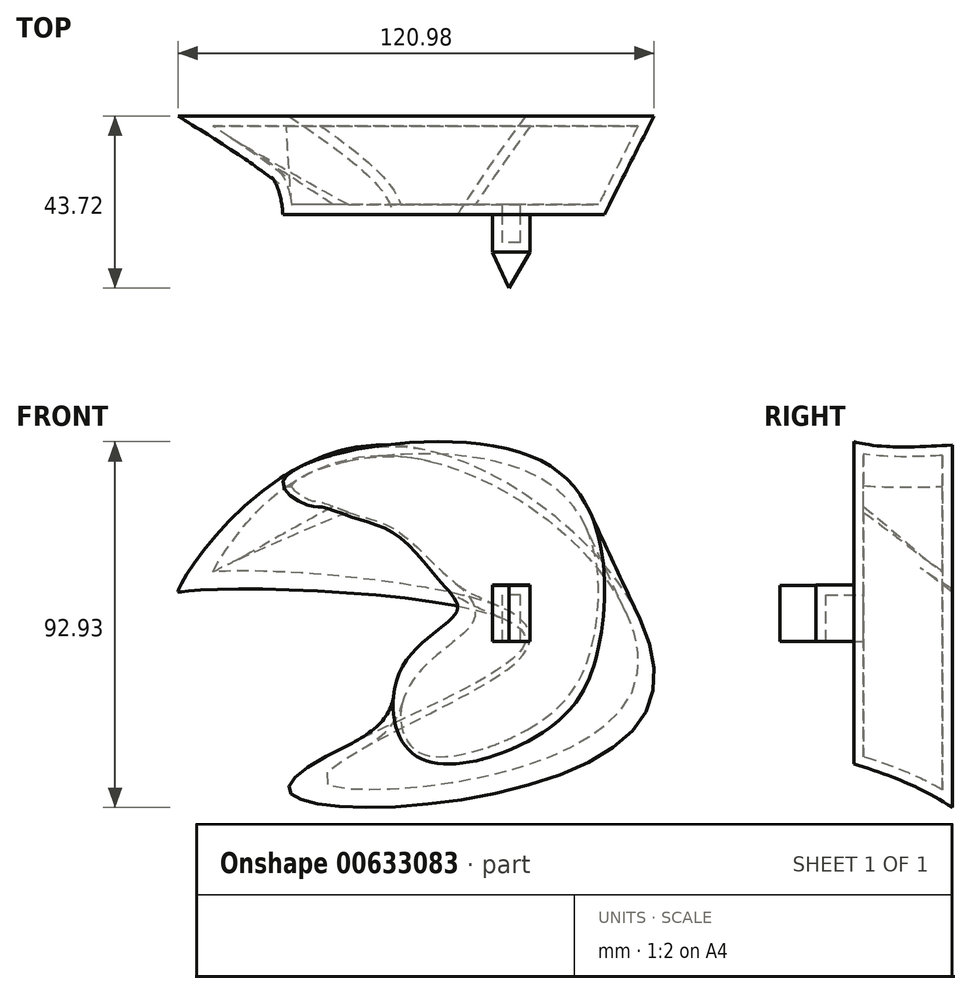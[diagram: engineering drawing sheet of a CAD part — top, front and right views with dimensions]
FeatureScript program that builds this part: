
annotation { "Feature Type Name" : "Feature", "Feature Type Description" : "" }
export const myFeature = defineFeature(function(context is Context, id is Id, definition is map)
    precondition{}
    {
        {
            var Q0;
            Q0=qCreatedBy(makeId("Front.planeOp"),FACE);
            var sketch = newSketch(context, id + "F0", { "sketchPlane" : qUnion([Q0])});
            skFitSpline(sketch, "E0", {"points": [v(-16.33, 40.2) * mm, v(-66.93, 3.34) * mm, v(-63.68, 3.15) * mm, v(21.3, -9.26) * mm, v(-38.86, -46.88) * mm, v(50.89, -29.31) * mm, v(-16.33, 40.2) * mm]});
            skSolve(sketch);
        }
        {
            var Q0;
            Q0=makeQuery(id+"F0.imprint","IMPRINT",FACE,{"disambiguationData":[TD([[makeQuery(id+"F0.imprint","IMPRINT",EDGE,{"derivedFrom":sQuery(id+"F0.wireOp",EDGE,"E0")}),1.0]])]});
            cPlane(context, id + "F1", {"entities" : qUnion([Q0]), "cplaneType" : CPlaneType.OFFSET, "offset" : 25 * mm, "width" : 150 * mm, "height" : 150 * mm});
        }
        {
            var Q0;
            Q0=qCreatedBy(id+"F1.planeOp",FACE);
            var sketch = newSketch(context, id + "F2", { "sketchPlane" : qUnion([Q0])});
            skFitSpline(sketch, "E1", {"points": [v(-40.27, 30.87) * mm, v(24.89, 36.37) * mm, v(40.37, -8.48) * mm, v(25.94, -32.7) * mm, v(-6.61, -38.72) * mm, v(-9.78, -15.81) * mm, v(3.9, -1.9) * mm, v(0, 5.1) * mm, v(-11.63, 17.45) * mm, v(-22.04, 21.6) * mm, v(-30.2, 24.38) * mm, v(-33.32, 24.7) * mm, v(-40.27, 30.87) * mm]});
            skSolve(sketch);
        }
        {
            var Q0;
            Q0=makeQuery(id+"F2.imprint","IMPRINT",FACE,{"disambiguationData":[TD([[makeQuery(id+"F2.imprint","IMPRINT",EDGE,{"derivedFrom":sQuery(id+"F2.wireOp",EDGE,"E1")}),-1.0]])]});
            var Q1;
            Q1=makeQuery(id+"F0.imprint","IMPRINT",FACE,{"disambiguationData":[TD([[makeQuery(id+"F0.imprint","IMPRINT",EDGE,{"derivedFrom":sQuery(id+"F0.wireOp",EDGE,"E0")}),1.0]])]});
            loft(context, id + "F3", {"sheetProfilesArray" : [{ "sheetProfileEntities" : qUnion([Q0]) }, { "sheetProfileEntities" : qUnion([Q1]) }]});
        }
        {
            var Q0;
            Q0=makeQuery(id+"F3.opLoft","CAP_FACE",FACE,{"disambiguationData":[OSD([makeQuery(id+"F2.imprint","IMPRINT",FACE,{"disambiguationData":[TD([[makeQuery(id+"F2.imprint","IMPRINT",EDGE,{"derivedFrom":sQuery(id+"F2.wireOp",EDGE,"E1")}),-1.0]])]})])],"isStart":true});
            var sketch = newSketch(context, id + "F4", { "sketchPlane" : qUnion([Q0])});
            skLineSegment(sketch, "E2.bottom", {"start": v(22.48, -9.74) * mm, "end": v(12.93, -9.74) * mm});
            skLineSegment(sketch, "E2.top", {"start": v(22.48, 4.57) * mm, "end": v(12.93, 4.57) * mm});
            skLineSegment(sketch, "E2.left", {"start": v(22.48, -9.74) * mm, "end": v(22.48, 4.57) * mm});
            skLineSegment(sketch, "E2.right", {"start": v(12.93, -9.74) * mm, "end": v(12.93, 4.57) * mm});
            skSolve(sketch);
        }
        {
            var Q0;
            Q0=makeQuery(id+"F4.imprint","IMPRINT",FACE,{"disambiguationData":[TD([[makeQuery(id+"F4.imprint","IMPRINT",EDGE,{"derivedFrom":sQuery(id+"F4.wireOp",EDGE,"E2.bottom")}),-1.0]])]});
            extrude(context, id + "F5", {"entities" : qUnion([Q0]), "operationType" : NewBodyOperationType.ADD, "depth" : 9.6 * mm, "offsetDistance" : 25 * mm});
        }
        {
            var Q0;
            Q0=makeQuery(id+"F5.opExtrude","SWEPT_FACE",FACE,{"disambiguationData":[OSD([sQuery(id+"F4.wireOp",EDGE,"E2.bottom")])]});
            cPlane(context, id + "F6", {"entities" : qUnion([Q0]), "cplaneType" : CPlaneType.OFFSET, "offset" : 0 * mm, "oppositeDirection" : true, "width" : 150 * mm, "height" : 150 * mm});
        }
        {
            var Q0;
            Q0=makeQuery(id+"F5.opExtrude","SWEPT_FACE",FACE,{"disambiguationData":[OSD([sQuery(id+"F4.wireOp",EDGE,"E2.bottom")])]});
            shell(context, id + "F7", {"entities" : qUnion([Q0]), "thickness" : 2.5 * mm});
        }
        {
            var Q0;
            Q0=qCreatedBy(id+"F6.planeOp",FACE);
            var sketch = newSketch(context, id + "F8", { "sketchPlane" : qUnion([Q0])});
            skLineSegment(sketch, "E3", {"start": v(12.92, 34.62) * mm, "end": v(17.12, 43.72) * mm});
            skLineSegment(sketch, "E4", {"start": v(17.12, 43.72) * mm, "end": v(22.48, 34.6) * mm});
            skLineSegment(sketch, "E5", {"start": v(22.48, 34.6) * mm, "end": v(12.92, 34.62) * mm});
            skSolve(sketch);
        }
        {
            var Q0;
            Q0=makeQuery(id+"F8.imprint","IMPRINT",FACE,{"disambiguationData":[TD([[makeQuery(id+"F8.imprint","IMPRINT",EDGE,{"derivedFrom":sQuery(id+"F8.wireOp",EDGE,"E3")}),-1.0]])]});
            extrude(context, id + "F9", {"entities" : qUnion([Q0]), "oppositeDirection" : true, "depth" : 14.3 * mm, "offsetDistance" : 25 * mm});
        }
    });
